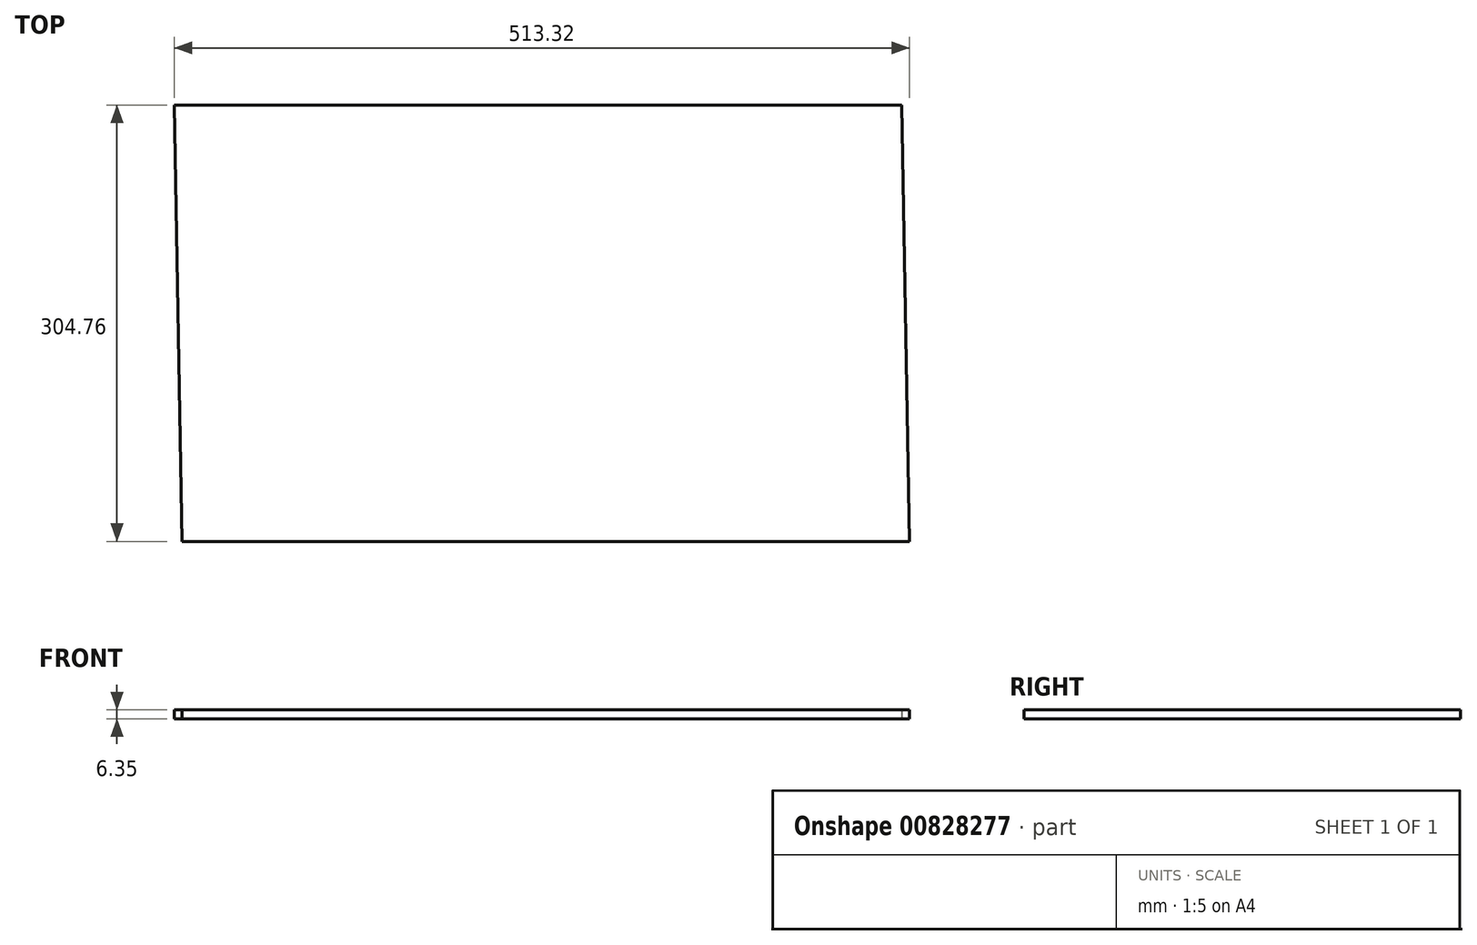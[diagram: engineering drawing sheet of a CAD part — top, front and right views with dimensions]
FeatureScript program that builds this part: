
annotation { "Feature Type Name" : "Feature", "Feature Type Description" : "" }
export const myFeature = defineFeature(function(context is Context, id is Id, definition is map)
    precondition{}
    {
        {
            var Q0;
            Q0=qCreatedBy(makeId("Top.planeOp"),FACE);
            var sketch = newSketch(context, id + "F0", { "sketchPlane" : qUnion([Q0])});
            skLineSegment(sketch, "E0.bottom", {"start": v(256.66, -152.38) * mm, "end": v(-251.34, -152.38) * mm});
            skLineSegment(sketch, "E0.top", {"start": v(251.34, 152.38) * mm, "end": v(-256.66, 152.38) * mm});
            skLineSegment(sketch, "E0.left", {"start": v(256.66, -152.38) * mm, "end": v(251.34, 152.38) * mm});
            skLineSegment(sketch, "E0.right", {"start": v(-251.34, -152.38) * mm, "end": v(-256.66, 152.38) * mm});
            skPoint(sketch, "E0.middle", {"position": v(0, 0) * mm});
            skSolve(sketch);
        }
        {
            var Q0;
            Q0 = qSketchRegion(id + "F0", true);
            extrude(context, id + "F1", {"entities" : qUnion([Q0]), "depth" : 6.35 * mm, "offsetDistance" : 25.4 * mm});
        }
    });
